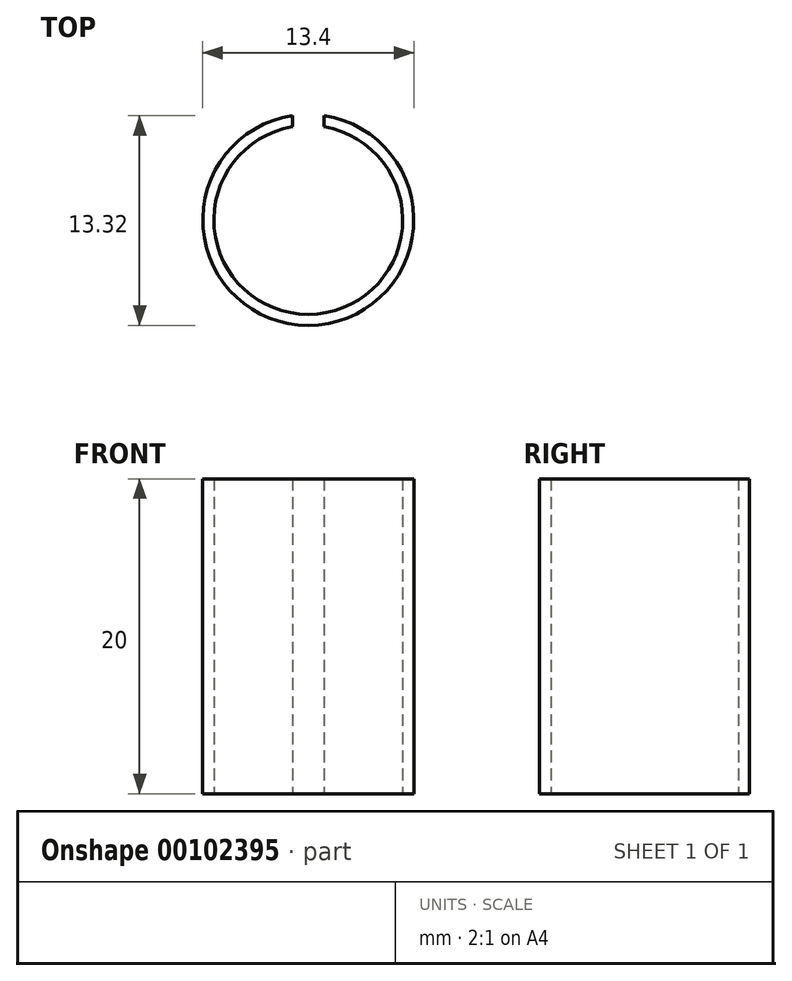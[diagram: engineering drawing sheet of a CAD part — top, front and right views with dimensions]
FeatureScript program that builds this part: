
annotation { "Feature Type Name" : "Feature", "Feature Type Description" : "" }
export const myFeature = defineFeature(function(context is Context, id is Id, definition is map)
    precondition{}
    {
        {
            var Q0;
            Q0=qCreatedBy(makeId("Top.planeOp"),FACE);
            var sketch = newSketch(context, id + "F0", { "sketchPlane" : qUnion([Q0])});
            skCircle(sketch, "E0", {"center": v(0, 0) * mm, "radius": 6.7 * mm});
            skCircle(sketch, "E1", {"center": v(0, 0) * mm, "radius": 6 * mm});
            skSolve(sketch);
        }
        {
            var Q0;
            Q0=qSketchRegion(id+"F0",true);
            extrude(context, id + "F1", {"entities" : qUnion([Q0]), "depth" : 20 * mm, "symmetric" : true});
        }
        {
            var Q0;
            Q0=qCreatedBy(makeId("Top.planeOp"),FACE);
            var sketch = newSketch(context, id + "F2", { "sketchPlane" : qUnion([Q0])});
            skLineSegment(sketch, "E2.bottom", {"start": v(-1, 6.7) * mm, "end": v(1, 6.7) * mm});
            skLineSegment(sketch, "E2.top", {"start": v(-1, 0) * mm, "end": v(1, 0) * mm});
            skLineSegment(sketch, "E2.left", {"start": v(-1, 6.7) * mm, "end": v(-1, 0) * mm});
            skLineSegment(sketch, "E2.right", {"start": v(1, 6.7) * mm, "end": v(1, 0) * mm});
            skSolve(sketch);
        }
        {
            var Q0;
            Q0=qSketchRegion(id+"F2",true);
            extrude(context, id + "F3", {"entities" : qUnion([Q0]), "operationType" : NewBodyOperationType.REMOVE, "endBound" : BoundingType.THROUGH_ALL, "oppositeDirection" : true, "depth" : 25 * mm, "hasSecondDirection" : true, "secondDirectionBound" : BoundingType.THROUGH_ALL, "secondDirectionOppositeDirection" : false, "secondDirectionDepth" : 25 * mm});
        }
    });
